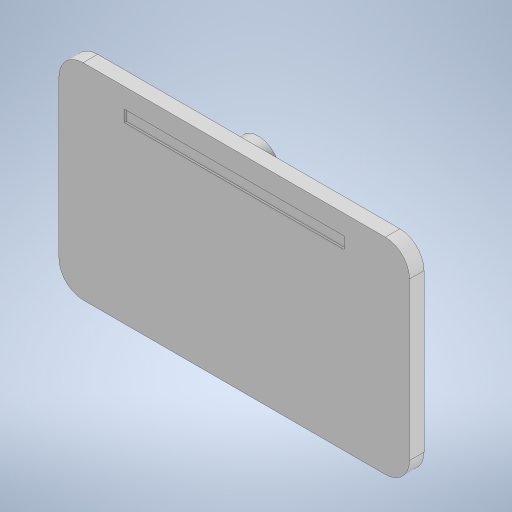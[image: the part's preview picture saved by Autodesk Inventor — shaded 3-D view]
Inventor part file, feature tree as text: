
AUTODESK INVENTOR PART (.ipt)
format: ipt  version: 2023 (Build 270158000, 158)  size: 283,648 bytes
history: native  units: mm
features: extrude x4, sketch x4, other x2, fillet x2, chamfer x1, mirror x1, projected_geometry x1
ambient origin geometry x8: Origin, YZ Plane, XZ Plane, XY Plane, X Axis, Y Axis, Z Axis, Center Point
bodies: Body1 (feature_tree)
feature tree (15):
  other  "솔리드1"
  extrude  "돌출1"  Depth=72.5mm
  extrude  "돌출2"  Depth=42.5mm
  fillet  "모깎기1"  Radius=3.0mm
  extrude  "돌출4"  Depth=4.0mm
  chamfer  "모따기1"  Distance=4.0mm
  other  "작업 평면1"
  extrude  "돌출5"  Depth=16.825mm
  mirror  "미러1"
  fillet  "모깎기2"  Radius=2.0mm
  sketch  "스케치1"
  sketch  "스케치2"
  projected_geometry  "투영된 루프1"
  sketch  "스케치5"
  sketch  "스케치6"
